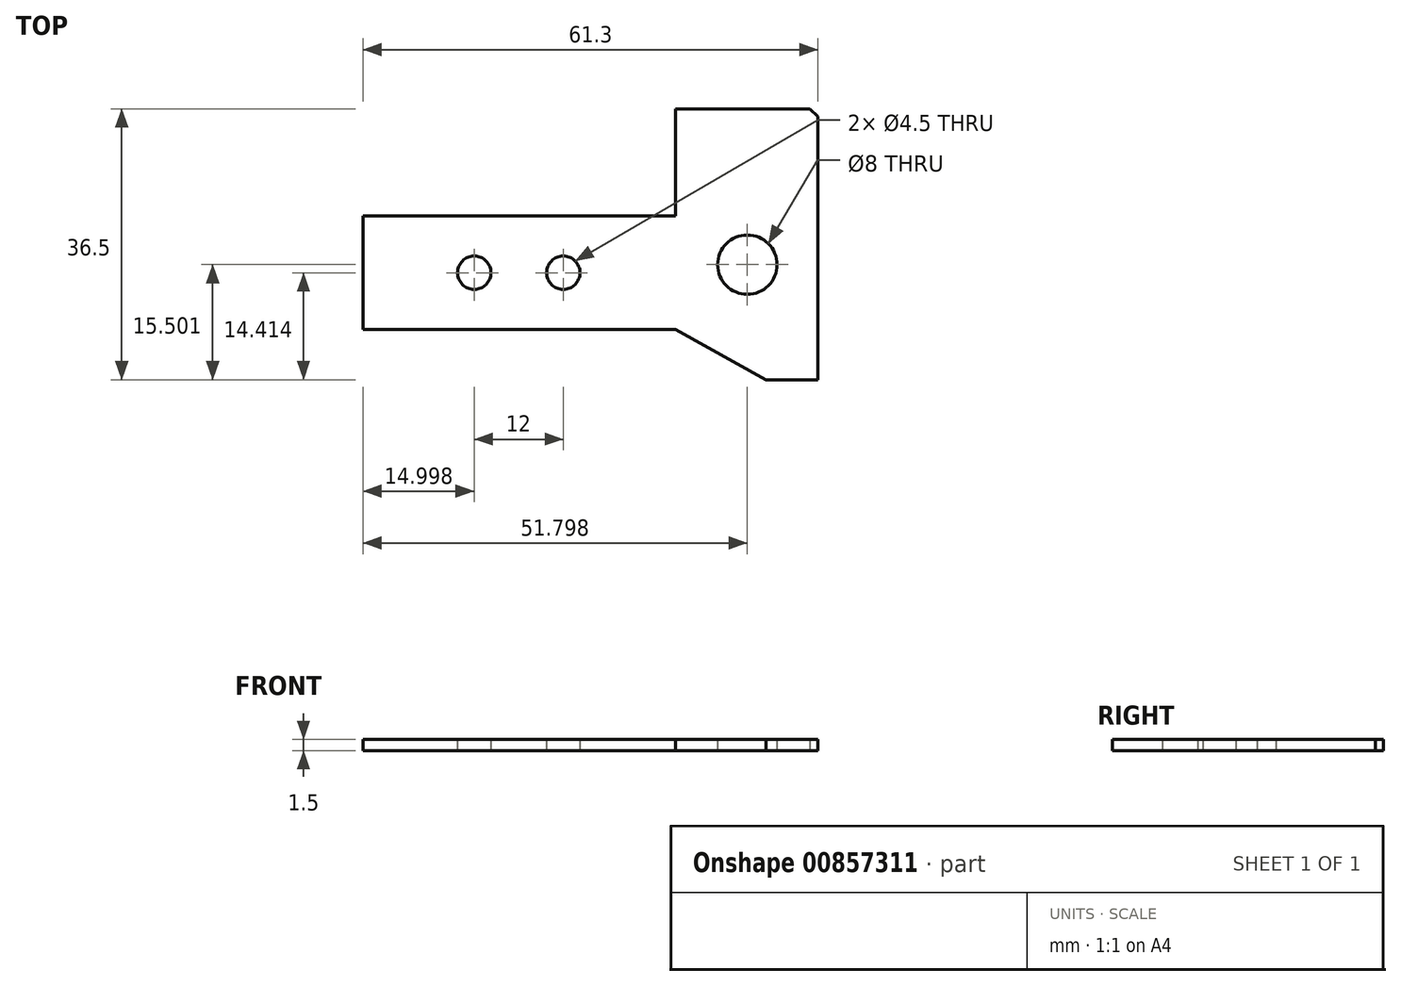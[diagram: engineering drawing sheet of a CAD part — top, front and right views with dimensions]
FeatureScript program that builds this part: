
annotation { "Feature Type Name" : "Feature", "Feature Type Description" : "" }
export const myFeature = defineFeature(function(context is Context, id is Id, definition is map)
    precondition{}
    {
        {
            var Q0;
            Q0=qCreatedBy(makeId("Top.planeOp"),FACE);
            var sketch = newSketch(context, id + "F0", { "sketchPlane" : qUnion([Q0])});
            skLineSegment(sketch, "E0.bottom", {"start": v(-49.62, 11.84) * mm, "end": v(-7.52, 11.84) * mm});
            skLineSegment(sketch, "E0.top", {"start": v(-49.62, -3.46) * mm, "end": v(-7.52, -3.46) * mm});
            skLineSegment(sketch, "E0.left", {"start": v(-49.62, 11.84) * mm, "end": v(-49.62, -3.46) * mm});
            skLineSegment(sketch, "E1", {"start": v(-49.62, 4.2) * mm, "end": v(52.8, 4.2) * mm, "construction": true});
            skLineSegment(sketch, "E2", {"start": v(-7.52, -3.46) * mm, "end": v(4.68, -10.22) * mm});
            skLineSegment(sketch, "E3", {"start": v(4.68, -10.22) * mm, "end": v(11.68, -10.22) * mm});
            skLineSegment(sketch, "E4", {"start": v(10.62, 26.28) * mm, "end": v(-7.52, 26.28) * mm});
            skLineSegment(sketch, "E5", {"start": v(-7.52, 26.28) * mm, "end": v(-7.52, 11.84) * mm});
            skLineSegment(sketch, "E6", {"start": v(11.68, -10.22) * mm, "end": v(11.68, 25.22) * mm});
            skLineSegment(sketch, "E7", {"start": v(11.68, 25.22) * mm, "end": v(10.62, 26.28) * mm});
            skCircle(sketch, "E8", {"center": v(-34.62, 4.2) * mm, "radius": 2.25 * mm});
            skCircle(sketch, "E9", {"center": v(-22.62, 4.2) * mm, "radius": 2.25 * mm});
            skCircle(sketch, "E10", {"center": v(2.18, 5.28) * mm, "radius": 4 * mm});
            skSolve(sketch);
        }
        {
            var Q0;
            Q0=makeQuery(id+"F0.imprint","IMPRINT",FACE,{"disambiguationData":[TD([[makeQuery(id+"F0.imprint","IMPRINT",EDGE,{"derivedFrom":sQuery(id+"F0.wireOp",EDGE,"E0.bottom")}),-1.0]])]});
            extrude(context, id + "F1", {"entities" : qUnion([Q0]), "depth" : 1.5 * mm, "offsetDistance" : 25 * mm});
        }
    });
